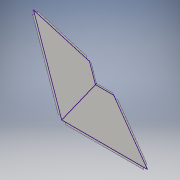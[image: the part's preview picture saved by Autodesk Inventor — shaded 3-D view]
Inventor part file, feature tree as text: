
AUTODESK INVENTOR PART (.ipt)
format: ipt  version: 2016 (Build 200138000, 138)  size: 180,736 bytes
history: native  units: in
note: dims shown in document units (in); Inventor stores cm internally (conversion verified against a paired STEP export)
features: sketch x3, extrude x2
ambient origin geometry x8: Origin, YZ Plane, XZ Plane, XY Plane, X Axis, Y Axis, Z Axis, Center Point
bodies: Body1 (feature_tree)
feature tree (5):
  extrude  "Extrusion2"  Depth=2.5in
  extrude  "Extrusion4"  Depth=6.5in
  sketch  "Sketch5"  dims[d5=7.9775in d31=0.8619in d32=0.8619in d33=0.3749in d34=0.3749in d35=0.375in d36=11.75in d37=0.8619in d38=2.5in d39=7.9779in d40=0.3749in d41=0.8619in d42=0.005in d43=0.0in d45=0.375in d46=0.2in d47=0.375in d48=0.375in d51=0.2in d68=0.3in d84=0.3in d86=0.005in d87=0.0in d89=90.0deg d90=0.5in d91=0.3in d93=90.0deg d94=0.5in d95=0.5in d97=0.5in d98=90.0deg d99=90.0deg d100=0.3in d101=0.5in d102=0.5in d103=0.3in d104=0.3in d105=0.5in d106=0.5in d107=0.3in d108=0.3in d109=90.0deg]
  sketch  "Sketch1"  dims[d1=11.75in d2=2.5in]
  sketch  "Sketch3"  dims[d3=6.5in d4=7.9775in]
